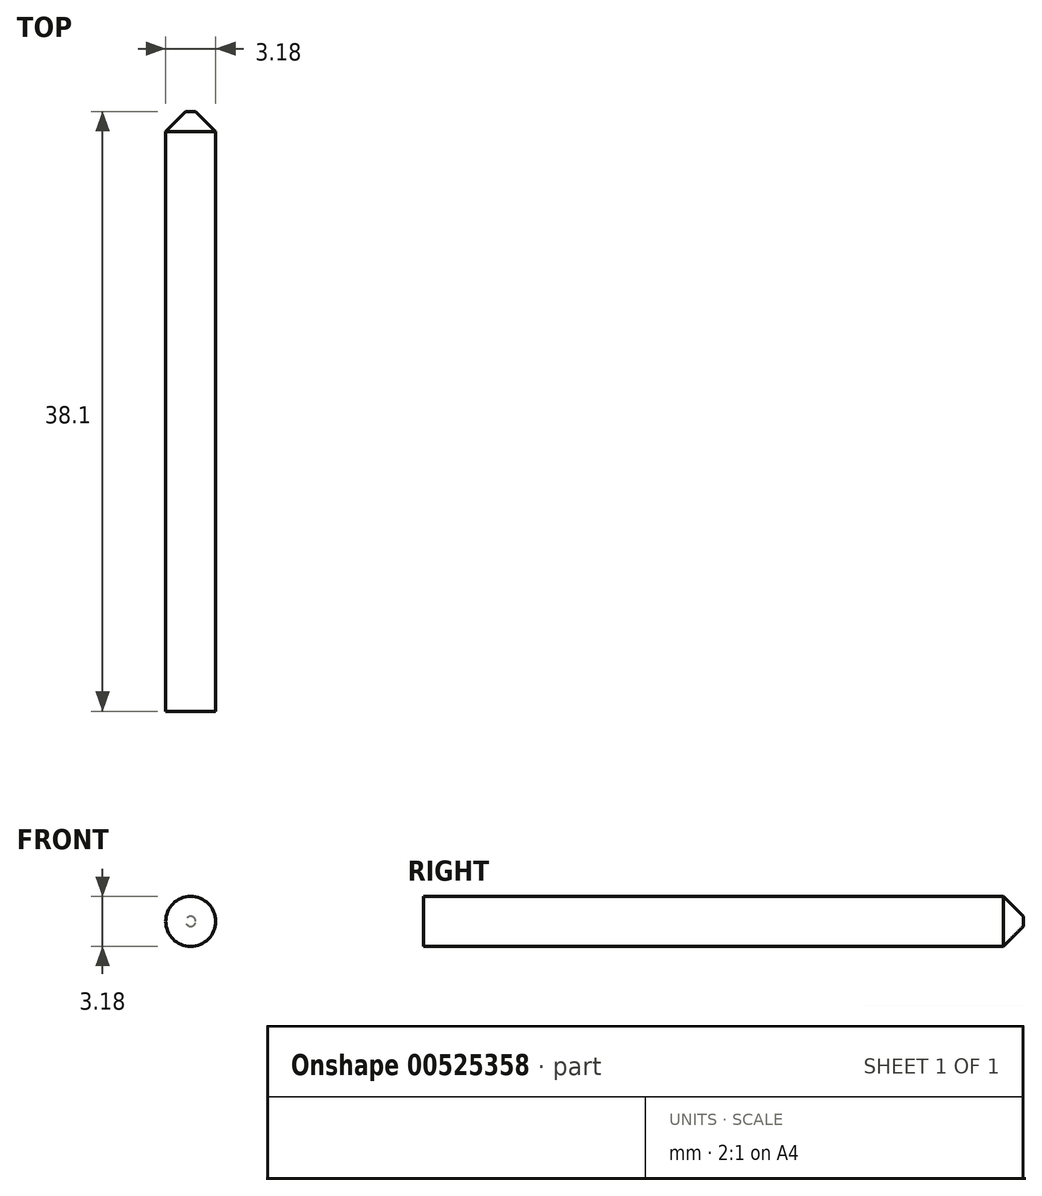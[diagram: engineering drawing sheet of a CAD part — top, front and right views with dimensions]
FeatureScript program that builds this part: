
annotation { "Feature Type Name" : "Feature", "Feature Type Description" : "" }
export const myFeature = defineFeature(function(context is Context, id is Id, definition is map)
    precondition{}
    {
        {
            var Q0;
            Q0=qCreatedBy(makeId("Front.planeOp"),FACE);
            var sketch = newSketch(context, id + "F0", { "sketchPlane" : qUnion([Q0])});
            skCircle(sketch, "E0", {"center": v(0, 0) * mm, "radius": 1.59 * mm});
            skSolve(sketch);
        }
        {
            var Q0;
            Q0 = qSketchRegion(id + "F0", true);
            extrude(context, id + "F1", {"entities" : qUnion([Q0]), "depth" : 38.1 * mm, "offsetDistance" : 25.4 * mm});
        }
        {
            var Q0;
            Q0=makeQuery(id+"F1.opExtrude","CAP_EDGE",EDGE,{"disambiguationData":[OSD([sQuery(id+"F0.wireOp",EDGE,"E0")])],"isStart":true});
            chamfer(context, id + "F2", {"entities" : qUnion([Q0]), "width" : 1.27 * mm, "tangentPropagation" : true});
        }
    });
